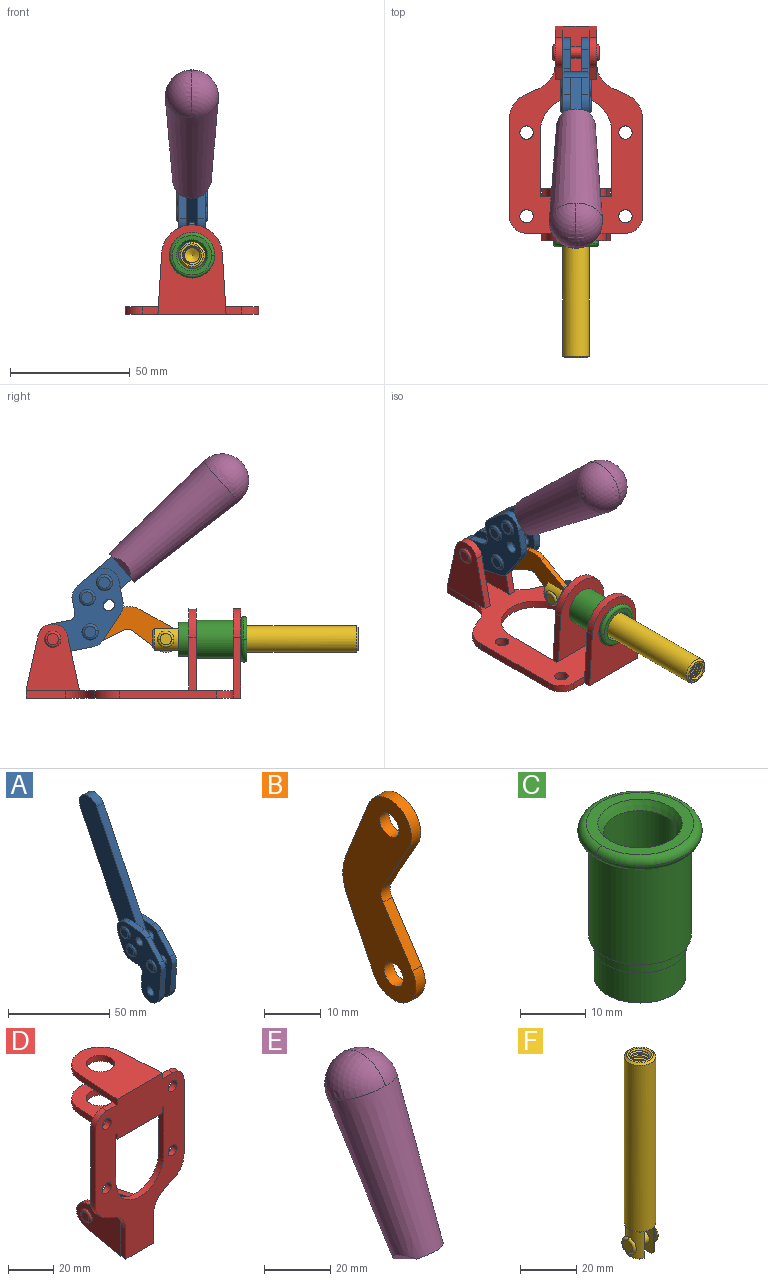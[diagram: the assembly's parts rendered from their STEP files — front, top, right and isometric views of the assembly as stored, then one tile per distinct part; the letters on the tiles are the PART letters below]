
ASSEMBLY  parts=6 mates=6
PART A: 59 faces, bbox 12.9x60.2x99.6 mm
  f0: torus R=2.39mm, axis (-1,0,0), area 14.9mm2, adj f20,f43,f51
  f1: torus R=2.39mm, axis (-1,0,0), area 14.9mm2, adj f19,f42,f51
  f2: torus R=2.39mm, axis (-1,0,0), area 14.9mm2, adj f18,f35,f51
  f3: torus R=2.39mm, axis (-1,0,0), area 14.9mm2, adj f14,f17,f23
  f4: torus R=2.39mm, axis (-1,0,0), area 14.9mm2, adj f13,f16,f23
  f5: torus R=2.39mm, axis (-1,0,0), area 14.9mm2, adj f12,f15,f23
  f6: cylinder r=2.39mm len=4.78mm, axis (1,0,0), area 46.5mm2, adj f48,f50,f51
  f7: cylinder r=2.39mm len=4.78mm, axis (1,0,0), area 46.5mm2, adj f50,f51
  f8: cylinder r=6.35mm len=12.68mm, axis (1,0,0), area 61.8mm2, adj f38,f39,f50,f51
  f9: cylinder r=2.39mm len=4.78mm, axis (-1,0,0), area 70.5mm2, adj f46,f50
  f10: cylinder r=2.39mm len=4.78mm, axis (-1,0,0), area 46.5mm2, adj f23,f45,f46
  f11: cylinder r=2.39mm len=4.78mm, axis (-1,0,0), area 46.5mm2, adj f23,f46
  f12: plane 4.78x4.78mm, normal (1,0,0), area 17.9mm2, adj f5,f15
  f13: plane 4.78x4.78mm, normal (1,0,0), area 17.9mm2, adj f4,f16
  f14: plane 4.78x4.78mm, normal (1,0,0), area 17.9mm2, adj f3,f17
  f15: torus R=2.39mm, axis (-1,0,0), area 14.9mm2, adj f5,f12,f23
  f16: torus R=2.39mm, axis (-1,0,0), area 14.9mm2, adj f4,f13,f23
  f17: torus R=2.39mm, axis (-1,0,0), area 14.9mm2, adj f3,f14,f23
  f18: plane 4.78x4.78mm, normal (-1,0,0), area 17.9mm2, adj f2,f35
  f19: plane 4.78x4.78mm, normal (-1,0,0), area 17.9mm2, adj f1,f42
  f20: plane 4.78x4.78mm, normal (-1,0,0), area 17.9mm2, adj f0,f43
  f21: plane 2.26x0.2mm, normal (1,0,0), area 0.2mm2, adj f31,f44
  f22: plane 2.26x0.2mm, normal (-1,0,0), area 0.2mm2, adj f41,f44
  f23: plane 39.37x30.77mm, normal (1,0,0), area 565.5mm2, adj f3,f4,f5,f10,f11,f15,f16,f17
  f24: cylinder r=6.1mm len=4.15mm, axis (-1,0,0), area 14.7mm2, adj f23,f25,f32,f46
  f25: plane 10.25x9.01mm, normal (0,-0.75,0.66), area 42.3mm2, adj f23,f24,f26,f46
  f26: cylinder r=6.35mm len=4.64mm, axis (-1,0,0), area 15.6mm2, adj f23,f25,f27,f46
  f27: plane 15.84x3.1mm, normal (0,-1,-0.07), area 49.2mm2, adj f23,f26,f28,f46
  f28: cylinder r=6.35mm len=12.68mm, axis (-1,0,0), area 61.8mm2, adj f23,f27,f29,f46
  f29: plane 8.11x3.1mm, normal (0,1,0.07), area 25.2mm2, adj f23,f28,f30,f46
  f30: cylinder r=3.05mm len=3.25mm, axis (-1,0,0), area 14.8mm2, adj f23,f29,f31,f46
  f31: plane 5.99x3.1mm, normal (0,0.07,-1), area 18.6mm2, adj f21,f23,f30,f44,f46
  f32: plane 9.5x3.1mm, normal (0,-0.07,1), area 29.5mm2, adj f23,f24,f33,f46,f47
  f33: cylinder r=6.1mm len=8.63mm, axis (-1,0,0), area 39.1mm2, adj f23,f32,f34,f47
  f34: plane 8.65x3.96mm, normal (0,0.91,-0.42), area 29.5mm2, adj f23,f33,f44,f47
  f35: torus R=2.39mm, axis (-1,0,0), area 14.9mm2, adj f2,f18,f51
  f36: plane 10.25x9.01mm, normal (0,-0.75,0.66), area 42.3mm2, adj f37,f49,f50,f51
  f37: cylinder r=6.35mm len=4.64mm, axis (1,0,0), area 15.6mm2, adj f36,f38,f50,f51
  f38: plane 15.84x3.1mm, normal (0,-1,-0.07), area 49.2mm2, adj f8,f37,f50,f51
  f39: plane 8.11x3.1mm, normal (0,1,0.07), area 25.2mm2, adj f8,f40,f50,f51
  f40: cylinder r=3.05mm len=3.25mm, axis (1,0,0), area 14.8mm2, adj f39,f41,f50,f51
  f41: plane 5.99x3.1mm, normal (0,0.07,-1), area 18.6mm2, adj f22,f40,f44,f50,f51
  f42: torus R=2.39mm, axis (-1,0,0), area 14.9mm2, adj f1,f19,f51
  f43: torus R=2.39mm, axis (-1,0,0), area 14.9mm2, adj f0,f20,f51
  f44: cylinder r=6.35mm len=12.12mm, axis (-1,0,0), area 128.9mm2, adj f21,f22,f23,f31,f34,f41,f46,f47
  f45: plane 2.65x1.35mm, normal (1,0,0), area 1mm2, adj f10,f55
  f46: plane 39.08x20.42mm, normal (-1,0,0), area 412.5mm2, adj f9,f10,f11,f24,f25,f26,f27,f28
  f47: plane 77.62x39.82mm, normal (1,0,0), area 850mm2, adj f32,f33,f34,f44,f53,f54,f55
  f48: plane 2.65x1.35mm, normal (-1,0,0), area 1mm2, adj f6,f55
  f49: cylinder r=6.1mm len=4.15mm, axis (1,0,0), area 14.7mm2, adj f36,f50,f51,f56
  f50: plane 39.08x20.42mm, normal (1,0,0), area 412.5mm2, adj f6,f7,f8,f9,f36,f37,f38,f39
  f51: plane 39.37x30.77mm, normal (-1,0,0), area 565.5mm2, adj f0,f1,f2,f6,f7,f8,f35,f36
  f52: plane 8.65x3.96mm, normal (0,0.91,-0.42), area 29.5mm2, adj f44,f51,f57,f58
  f53: plane 68.49x33.4mm, normal (0,0.9,-0.44), area 358.1mm2, adj f44,f47,f54,f58
  f54: cylinder r=6.35mm len=12.06mm, axis (1,0,0), area 93.7mm2, adj f47,f53,f55,f58
  f55: plane 68.49x33.4mm, normal (0,-0.9,0.44), area 358.1mm2, adj f44,f45,f46,f47,f48,f50,f54,f58
  f56: plane 9.5x3.1mm, normal (0,-0.07,1), area 29.5mm2, adj f49,f50,f51,f57,f58
  f57: cylinder r=6.1mm len=8.63mm, axis (1,0,0), area 39.1mm2, adj f51,f52,f56,f58
  f58: plane 77.62x39.82mm, normal (-1,0,0), area 850mm2, adj f44,f52,f53,f54,f55,f56,f57
PART B: 12 faces, bbox 2.3x18.2x42.8 mm
  f0: cylinder r=2.4mm len=4.8mm, axis (1,0,0), area 34.9mm2, adj f4,f11
  f1: cylinder r=10.41mm len=8.47mm, axis (1,0,0), area 20.2mm2, adj f4,f9,f10,f11
  f2: cylinder r=3.05mm len=3.16mm, axis (1,0,0), area 7.7mm2, adj f4,f6,f7,f11
  f3: cylinder r=2.4mm len=4.8mm, axis (1,0,0), area 34.9mm2, adj f4,f11
  f4: plane 42.81x18.23mm, normal (-1,0,0), area 414.1mm2, adj f0,f1,f2,f3,f5,f6,f7,f8
  f5: cylinder r=5.54mm len=10.67mm, axis (1,0,0), area 41.8mm2, adj f4,f6,f10,f11
  f6: plane 11.66x6.53mm, normal (0,-0.87,-0.49), area 30.9mm2, adj f2,f4,f5,f11
  f7: plane 11.17x7.33mm, normal (0,-0.84,0.55), area 30.9mm2, adj f2,f4,f8,f11
  f8: cylinder r=5.54mm len=10.51mm, axis (1,0,0), area 41.8mm2, adj f4,f7,f9,f11
  f9: plane 13.67x6.67mm, normal (0,0.9,-0.44), area 35.1mm2, adj f1,f4,f8,f11
  f10: plane 14.1x5.7mm, normal (0,0.93,0.37), area 35.1mm2, adj f1,f4,f5,f11
  f11: plane 42.81x18.23mm, normal (1,0,0), area 414.1mm2, adj f0,f1,f2,f3,f5,f6,f7,f8
PART C: 15 faces, bbox 20.6x20.6x28.7 mm
  f0: torus R=8.26mm, axis (0,0,1), area 56.8mm2, adj f1,f10,f12
  f1: torus R=8.26mm, axis (0,0,1), area 56.8mm2, adj f0,f6,f13
  f2: cylinder r=5.59mm len=25.91mm, axis (0,0,1), area 909.6mm2, adj f3,f4
  f3: cone r=6.86mm half-angle=45deg, axis (0,0,-1), area 70.2mm2, adj f2,f14
  f4: cone r=6.47mm half-angle=30deg, axis (0,0,1), area 66.7mm2, adj f2,f13
  f5: cylinder r=7.04mm len=14.07mm, axis (0,0,1), area 252.6mm2, adj f11,f14
  f6: torus R=8.26mm, axis (0,0,1), area 56.8mm2, adj f1,f12,f13
  f7: cylinder r=7.16mm len=14.33mm, axis (0,0,1), area 91.5mm2, adj f9,f11
  f8: cylinder r=7.86mm len=18.42mm, axis (0,0,1), area 909.6mm2, adj f9,f10
  f9: plane 15.72x15.72mm, normal (0,0,-1), area 33mm2, adj f7,f8
  f10: plane 16.51x16.51mm, normal (0,0,-1), area 19.9mm2, adj f0,f8,f12
  f11: plane 14.33x14.33mm, normal (0,0,-1), area 5.7mm2, adj f5,f7
  f12: torus R=8.26mm, axis (0,0,1), area 56.8mm2, adj f0,f6,f10
  f13: plane 16.51x16.51mm, normal (0,0,1), area 82.7mm2, adj f1,f4,f6
  f14: plane 14.07x14.07mm, normal (0,0,-1), area 7.8mm2, adj f3,f5
PART D: 55 faces, bbox 55.7x37.4x89.8 mm
  f0: torus R=2.41mm, axis (-1,0,0), area 15mm2, adj f11,f15,f25
  f1: torus R=2.41mm, axis (-1,0,0), area 15mm2, adj f10,f12,f22
  f2: cylinder r=2.78mm len=5.56mm, axis (0,-1,0), area 54.2mm2, adj f30,f54
  f3: cylinder r=14.99mm len=29.97mm, axis (0,-1,0), area 145.9mm2, adj f30,f49,f53,f54
  f4: cylinder r=2.78mm len=5.56mm, axis (0,-1,0), area 54.2mm2, adj f30,f54
  f5: cylinder r=2.78mm len=5.56mm, axis (0,-1,0), area 54.2mm2, adj f30,f54
  f6: cylinder r=2.78mm len=5.56mm, axis (0,-1,0), area 54.2mm2, adj f30,f54
  f7: cylinder r=6.35mm len=12.7mm, axis (0,0,1), area 123.6mm2, adj f27,f51
  f8: cylinder r=6.35mm len=12.7mm, axis (0,0,-1), area 124.7mm2, adj f21,f35
  f9: cylinder r=2.41mm len=11.18mm, axis (-1,0,0), area 169.4mm2, adj f16,f19
  f10: plane 4.83x4.83mm, normal (1,0,0), area 18.3mm2, adj f1,f12
  f11: plane 4.83x4.83mm, normal (-1,0,0), area 18.3mm2, adj f0,f15
  f12: torus R=2.41mm, axis (-1,0,0), area 15mm2, adj f1,f10,f22
  f13: cylinder r=6.35mm len=12.41mm, axis (1,0,0), area 53.4mm2, adj f18,f19,f22,f23
  f14: cylinder r=6.35mm len=12.41mm, axis (-1,0,0), area 53.4mm2, adj f16,f17,f24,f25
  f15: torus R=2.41mm, axis (-1,0,0), area 15mm2, adj f0,f11,f25
  f16: plane 27.86x22.35mm, normal (1,0,0), area 425.4mm2, adj f9,f14,f17,f24,f30
  f17: plane 22.86x4.97mm, normal (0,0.21,0.98), area 72.5mm2, adj f14,f16,f25,f30
  f18: plane 22.86x4.97mm, normal (0,0.21,0.98), area 72.5mm2, adj f13,f19,f22,f30
  f19: plane 27.86x22.35mm, normal (-1,0,0), area 425.4mm2, adj f9,f13,f18,f23,f30
  f20: cylinder r=12.7mm len=25.35mm, axis (0,0,-1), area 119.8mm2, adj f21,f34,f35,f36
  f21: plane 34.21x28.07mm, normal (0,0,-1), area 702.4mm2, adj f8,f20,f30,f34,f36
  f22: plane 27.96x22.45mm, normal (1,0,0), area 407.2mm2, adj f1,f12,f13,f18,f23,f30,f42,f43
  f23: plane 22.86x4.97mm, normal (0,0.21,-0.98), area 72.5mm2, adj f13,f19,f22,f44
  f24: plane 22.86x4.97mm, normal (0,0.21,-0.98), area 72.5mm2, adj f14,f16,f25,f44
  f25: plane 27.86x22.35mm, normal (-1,0,0), area 407.1mm2, adj f0,f14,f15,f17,f24,f30,f45,f46
  f26: plane 3.1x0.95mm, normal (0,0,-1), area 2.7mm2, adj f30,f49,f50,f54
  f27: plane 34.21x28.07mm, normal (0,0,1), area 702.4mm2, adj f7,f28,f30,f50,f52
  f28: cylinder r=12.7mm len=25.35mm, axis (0,0,1), area 118.8mm2, adj f27,f50,f51,f52
  f29: plane 3.1x0.95mm, normal (0,0,-1), area 2.7mm2, adj f30,f52,f53,f54
  f30: plane 86.54x55.63mm, normal (0,1,0), area 2362.9mm2, adj f2,f3,f4,f5,f6,f16,f17,f18
  f31: plane 40.56x3.1mm, normal (-1,0,0), area 125.7mm2, adj f30,f32,f48,f54
  f32: cylinder r=7.11mm len=7.11mm, axis (0,-1,0), area 34.6mm2, adj f30,f31,f33,f54
  f33: plane 6.67x3.1mm, normal (0,0,1), area 20.4mm2, adj f30,f32,f34,f54
  f34: plane 25.39x3.13mm, normal (-1,0.06,0), area 79.5mm2, adj f20,f21,f33,f35,f54
  f35: plane 37.31x28.45mm, normal (0,0,1), area 789.9mm2, adj f8,f20,f34,f36,f54
  f36: plane 25.39x3.13mm, normal (1,0.06,0), area 79.5mm2, adj f20,f21,f35,f37,f54
  f37: plane 6.67x3.1mm, normal (0,0,1), area 20.4mm2, adj f30,f36,f38,f54
  f38: cylinder r=7.11mm len=7.11mm, axis (0,-1,0), area 34.6mm2, adj f30,f37,f39,f54
  f39: plane 40.56x3.1mm, normal (1,0,0), area 125.7mm2, adj f30,f38,f40,f54
  f40: cylinder r=11.18mm len=10.16mm, axis (0,-1,0), area 39.5mm2, adj f30,f39,f41,f54
  f41: plane 6.09x3.1mm, normal (0.42,0,-0.91), area 20.8mm2, adj f30,f40,f42,f54
  f42: cylinder r=11.18mm len=9.41mm, axis (0,-1,0), area 37.2mm2, adj f22,f30,f41,f43,f54
  f43: plane 16.5x3.1mm, normal (1,0,0), area 51.1mm2, adj f22,f42,f44,f54
  f44: plane 17.37x3.1mm, normal (0,0,-1), area 53.8mm2, adj f23,f24,f30,f43,f45,f54
  f45: plane 16.5x3.1mm, normal (-1,0,0), area 51.1mm2, adj f25,f44,f46,f54
  f46: cylinder r=11.18mm len=9.41mm, axis (0,-1,0), area 37.2mm2, adj f25,f30,f45,f47,f54
  f47: plane 6.09x3.1mm, normal (-0.42,0,-0.91), area 20.8mm2, adj f30,f46,f48,f54
  f48: cylinder r=11.18mm len=10.16mm, axis (0,-1,0), area 39.5mm2, adj f30,f31,f47,f54
  f49: plane 26.54x3.1mm, normal (-1,0,0), area 82.3mm2, adj f3,f26,f30,f54
  f50: plane 25.39x3.1mm, normal (1,0.06,0), area 78.8mm2, adj f26,f27,f28,f51,f54
  f51: plane 37.31x28.45mm, normal (0,0,-1), area 789.9mm2, adj f7,f28,f50,f52,f54
  f52: plane 25.39x3.1mm, normal (-1,0.06,0), area 78.8mm2, adj f27,f28,f29,f51,f54
  f53: plane 26.54x3.1mm, normal (1,0,0), area 82.3mm2, adj f3,f29,f30,f54
  f54: plane 89.66x55.63mm, normal (0,-1,0), area 2678.5mm2, adj f2,f3,f4,f5,f6,f26,f29,f31
PART E: 11 faces, bbox 22.3x42.6x64.5 mm
  f0: sphere r=11.13mm, area 411.4mm2, adj f1,f8
  f1: cone r=11.11mm half-angle=3.3deg, axis (0,0.44,0.9), area 3251.8mm2, adj f0,f7,f8,f9,f10
  f2: cylinder r=6.16mm len=11.7mm, axis (1,0,0), area 89.5mm2, adj f3,f4,f5,f6
  f3: plane 60.23x36.75mm, normal (-1,0,0), area 763.6mm2, adj f2,f4,f6,f10
  f4: plane 51.37x25.05mm, normal (0,0.9,-0.44), area 264.2mm2, adj f2,f3,f5,f10
  f5: plane 60.23x36.75mm, normal (1,0,0), area 763.6mm2, adj f2,f4,f6,f10
  f6: plane 51.37x25.05mm, normal (0,-0.9,0.44), area 264.2mm2, adj f2,f3,f5,f10
  f7: plane 9.95x5.95mm, normal (0.71,-0.31,-0.64), area 25.8mm2, adj f1,f10
  f8: sphere r=11.13mm, area 411.4mm2, adj f0,f1
  f9: plane 9.95x5.95mm, normal (-0.71,-0.31,-0.64), area 25.8mm2, adj f1,f10
  f10: plane 14.27x11.38mm, normal (0,-0.44,-0.9), area 106.7mm2, adj f1,f3,f4,f5,f6,f7,f9
PART F: 48 faces, bbox 12.6x11.1x86.1 mm
  f0: torus R=2.41mm, axis (-1,0,0), area 15mm2, adj f30,f32,f34
  f1: torus R=2.41mm, axis (-1,0,0), area 15mm2, adj f29,f31,f33
  f2: cylinder r=5.54mm len=72.39mm, axis (0,0,1), area 2518.5mm2, adj f3,f4,f42,f43
  f3: cone r=5.54mm half-angle=45deg, axis (0,0,1), area 7.6mm2, adj f2,f5,f41
  f4: cone r=5.54mm half-angle=45deg, axis (0,0,-1), area 34.9mm2, adj f2,f39
  f5: cylinder r=5.08mm len=11.48mm, axis (0,0,1), area 108.3mm2, adj f3,f7,f8,f41
  f6: cylinder r=2.41mm len=4.83mm, axis (-1,0,0), area 71.2mm2, adj f40,f41
  f7: cylinder r=2.41mm len=4.83mm, axis (-1,0,0), area 7.6mm2, adj f5,f34
  f8: cone r=5.08mm half-angle=45deg, axis (0,0,1), area 10.6mm2, adj f5,f37,f41
  f9: cone r=3.98mm half-angle=45deg, axis (0,0,1), area 17.6mm2, adj f27,f39,f45,f46,f47
  f10: cylinder r=2.41mm len=4.83mm, axis (-1,0,0), area 7.6mm2, adj f33,f38
  f11: cylinder r=3.2mm len=6.4mm, axis (0,0,1), area 78.4mm2, adj f12,f28,f44,f45,f47
  f12: cylinder r=3.2mm len=6.4mm, axis (0,0,1), area 10.5mm2, adj f11,f13,f45,f47
  f13: cylinder r=3.2mm len=6.4mm, axis (0,0,1), area 10.5mm2, adj f12,f14,f45,f47
  f14: cylinder r=3.2mm len=6.4mm, axis (0,0,1), area 10.5mm2, adj f13,f15,f45,f47
  f15: cylinder r=3.2mm len=6.4mm, axis (0,0,1), area 10.5mm2, adj f14,f16,f45,f47
  f16: cylinder r=3.2mm len=6.4mm, axis (0,0,1), area 10.5mm2, adj f15,f17,f45,f47
  f17: cylinder r=3.2mm len=6.4mm, axis (0,0,1), area 10.5mm2, adj f16,f18,f45,f47
  f18: cylinder r=3.2mm len=6.4mm, axis (0,0,1), area 10.5mm2, adj f17,f19,f45,f47
  f19: cylinder r=3.2mm len=6.4mm, axis (0,0,1), area 10.5mm2, adj f18,f20,f45,f47
  f20: cylinder r=3.2mm len=6.4mm, axis (0,0,1), area 10.5mm2, adj f19,f21,f45,f47
  f21: cylinder r=3.2mm len=6.4mm, axis (0,0,1), area 10.5mm2, adj f20,f22,f45,f47
  f22: cylinder r=3.2mm len=6.4mm, axis (0,0,1), area 10.5mm2, adj f21,f23,f45,f47
  f23: cylinder r=3.2mm len=6.4mm, axis (0,0,1), area 10.5mm2, adj f22,f24,f45,f47
  f24: cylinder r=3.2mm len=6.4mm, axis (0,0,1), area 10.5mm2, adj f23,f25,f45,f47
  f25: cylinder r=3.2mm len=6.4mm, axis (0,0,1), area 10.5mm2, adj f24,f26,f45,f47
  f26: cylinder r=3.2mm len=6.4mm, axis (0,0,1), area 10.5mm2, adj f25,f27,f45,f47
  f27: cylinder r=3.2mm len=6.4mm, axis (0,0,1), area 7.4mm2, adj f9,f26,f45,f47
  f28: cone r=3.2mm half-angle=60deg, axis (0,0,1), area 37.2mm2, adj f11
  f29: plane 4.83x4.83mm, normal (-1,0,0), area 18.3mm2, adj f1,f31
  f30: plane 4.83x4.83mm, normal (1,0,0), area 18.3mm2, adj f0,f32
  f31: torus R=2.41mm, axis (-1,0,0), area 15mm2, adj f1,f29,f33
  f32: torus R=2.41mm, axis (-1,0,0), area 15mm2, adj f0,f30,f34
  f33: plane 6.83x6.83mm, normal (1,0,0), area 18.3mm2, adj f1,f10,f31
  f34: plane 6.83x6.83mm, normal (-1,0,0), area 18.3mm2, adj f0,f7,f32
  f35: cone r=5.08mm half-angle=45deg, axis (0,0,1), area 10.6mm2, adj f36,f38,f40
  f36: plane 7.25x1.97mm, normal (0,0,-1), area 10mm2, adj f35,f40
  f37: plane 7.25x1.97mm, normal (0,0,-1), area 10mm2, adj f8,f41
  f38: cylinder r=5.08mm len=11.48mm, axis (0,0,1), area 108.3mm2, adj f10,f35,f40,f42
  f39: plane 9.55x9.55mm, normal (0,0,1), area 22mm2, adj f4,f9
  f40: plane 12.76x10.09mm, normal (1,0,0), area 95.7mm2, adj f6,f35,f36,f38,f42,f43
  f41: plane 12.76x10.09mm, normal (-1,0,0), area 95.7mm2, adj f3,f5,f6,f8,f37,f43
  f42: cone r=5.54mm half-angle=45deg, axis (0,0,1), area 7.6mm2, adj f2,f38,f40
  f43: plane 11.07x4.7mm, normal (0,0,-1), area 50.4mm2, adj f2,f40,f41
  f44: plane 0.89x0.62mm, normal (-1,0,0), area 0.3mm2, adj f11,f45,f46,f47
  f45: bspline ~24.8x7.63mm, area 266.6mm2, adj f9,f11,f12,f13,f14,f15,f16,f17
  f46: bspline ~24.87x7.63mm, area 73.6mm2, adj f9,f44,f45,f47
  f47: bspline ~24.98x7.63mm, area 272.5mm2, adj f9,f11,f12,f13,f14,f15,f16,f17
PLACE A rot(axis=(1,0,0),75deg) t=(0,4.15,9.14)mm
PLACE B rot(axis=(1,0,0),97.5deg) t=(0,12.88,2.22)mm
PLACE C rot(axis=(1,0,0),90deg) t=(0,9.43,0)mm
PLACE D rot(axis=(1,0,0),90deg) t=(0,9.43,0)mm fixed
PLACE E rot(axis=(1,0,0),75deg) t=(-0.04,4.15,9.14)mm
PLACE F rot(axis=(1,0,0),90deg) t=(0,9.81,0)mm
MATE revolute B.f5 <-> F.f6  axis (1,0,0) through (0,-5.67,24.61)mm
MATE slider F.f2 <-> C.f2  axis (0,-1,0) through (0,-48.97,24.61)mm
MATE revolute B.f3 <-> A.f4  axis (1,0,0) through (0,25.94,27.64)mm
MATE fastened E.f2 <-> A.f54  axis (1,0,0) through (-2.35,-30.37,91.94)mm
MATE fastened C.f2 <-> D.f7  axis (0,-1,0) through (0,-36.96,24.61)mm
MATE revolute D.f0 <-> A.f7  axis (-1,0,0) through (0,41.52,24.61)mm
